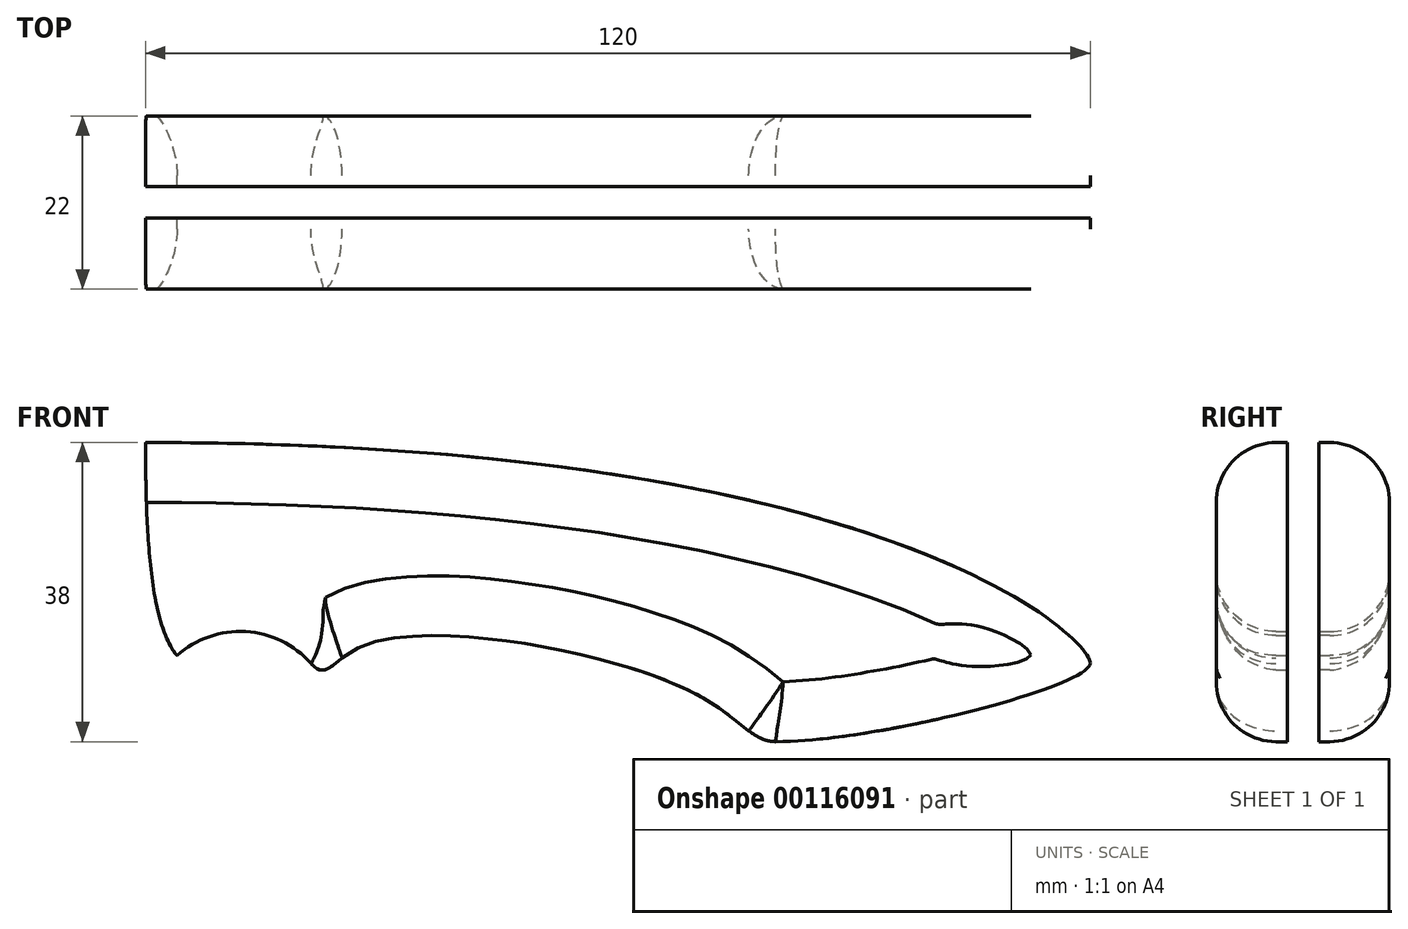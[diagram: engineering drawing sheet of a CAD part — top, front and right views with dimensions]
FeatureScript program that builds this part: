
annotation { "Feature Type Name" : "Feature", "Feature Type Description" : "" }
export const myFeature = defineFeature(function(context is Context, id is Id, definition is map)
    precondition{}
    {
        {
            var Q0;
            Q0=qCreatedBy(makeId("Front.planeOp"),FACE);
            var sketch = newSketch(context, id + "F0", { "sketchPlane" : qUnion([Q0])});
            skLineSegment(sketch, "E0.bottom", {"start": v(0, 0) * mm, "end": v(230, 0) * mm});
            skLineSegment(sketch, "E0.top", {"start": v(0, -38) * mm, "end": v(230, -38) * mm});
            skLineSegment(sketch, "E0.left", {"start": v(0, 0) * mm, "end": v(0, -38) * mm});
            skLineSegment(sketch, "E0.right", {"start": v(230, 0) * mm, "end": v(230, -38) * mm});
            skSolve(sketch);
        }
        {
            var Q0;
            Q0=makeQuery(id+"F0.imprint","IMPRINT",FACE,{"disambiguationData":[TD([[makeQuery(id+"F0.imprint","IMPRINT",EDGE,{"derivedFrom":sQuery(id+"F0.wireOp",EDGE,"E0.bottom")}),-1.0]])]});
            var sketch = newSketch(context, id + "F1", { "sketchPlane" : qUnion([Q0])});
            skLineSegment(sketch, "E1", {"start": v(0, 0) * mm, "end": v(0, -12) * mm});
            skLineSegment(sketch, "E2", {"start": v(110, 0) * mm, "end": v(230, 0) * mm});
            skFitSpline(sketch, "E3", {"points": [v(0, -12) * mm, v(110, 0) * mm], "startDerivative": vector(36.23, 12.3) * mm, "endDerivative": vector(240, 0) * mm});
            skFitSpline(sketch, "E4", {"points": [v(0, -12) * mm, v(110, -38) * mm], "startDerivative": vector(39.03, -50.57) * mm, "endDerivative": vector(165, 0) * mm});
            skFitSpline(sketch, "E5", {"points": [v(110, 0) * mm, v(230, -28) * mm], "startDerivative": vector(285, 0) * mm, "endDerivative": vector(0, -9) * mm});
            skLineSegment(sketch, "E6", {"start": v(110, -38) * mm, "end": v(110, -36) * mm});
            skLineSegment(sketch, "E7", {"start": v(110, -36) * mm, "end": v(122, -36) * mm, "construction": true});
            skArc(sketch, "E8", {"start": v(131, -28.06) * mm, "mid": v(117.76, -24.78) * mm, "end": v(110, -36) * mm});
            skLineSegment(sketch, "E9", {"start": v(131, -28.06) * mm, "end": v(132.98, -30.31) * mm});
            skFitSpline(sketch, "E10", {"points": [v(190, -38) * mm, v(180, -32) * mm, v(137, -26.06) * mm, v(131, -28.06) * mm], "startDerivative": vector(-33, 0) * mm, "endDerivative": vector(-29.63, 33.6) * mm});
            skFitSpline(sketch, "E11", {"points": [v(230, -28) * mm, v(190, -38) * mm], "startDerivative": vector(0, -9) * mm, "endDerivative": vector(-39, 0) * mm});
            skLineSegment(sketch, "E12", {"start": v(110, -28.06) * mm, "end": v(131, -28.06) * mm, "construction": true});
            skLineSegment(sketch, "E13", {"start": v(131, -26.06) * mm, "end": v(137, -26.06) * mm, "construction": true});
            skLineSegment(sketch, "E14", {"start": v(131, -28.06) * mm, "end": v(131, -26.06) * mm, "construction": true});
            skLineSegment(sketch, "E15", {"start": v(190, -38) * mm, "end": v(187, -38) * mm});
            skLineSegment(sketch, "E16", {"start": v(190, -32) * mm, "end": v(180, -32) * mm, "construction": true});
            skLineSegment(sketch, "E17", {"start": v(190, -38) * mm, "end": v(190, -32) * mm, "construction": true});
            skLineSegment(sketch, "E18", {"start": v(190, -38) * mm, "end": v(203, -38) * mm, "construction": true});
            skLineSegment(sketch, "E19", {"start": v(190, -38) * mm, "end": v(230, -38) * mm, "construction": true});
            skLineSegment(sketch, "E20", {"start": v(230, -28) * mm, "end": v(230, -25) * mm, "construction": true});
            skLineSegment(sketch, "E21", {"start": v(230, -28) * mm, "end": v(230, -31) * mm, "construction": true});
            skLineSegment(sketch, "E22", {"start": v(230, -28) * mm, "end": v(230, -38) * mm, "construction": true});
            skLineSegment(sketch, "E23", {"start": v(110, 0) * mm, "end": v(30, 0) * mm, "construction": true});
            skLineSegment(sketch, "E24", {"start": v(0, 0) * mm, "end": v(110, 0) * mm, "construction": true});
            skLineSegment(sketch, "E25", {"start": v(110, 0) * mm, "end": v(205, 0) * mm});
            skLineSegment(sketch, "E26", {"start": v(0, -12) * mm, "end": v(12.08, -7.9) * mm});
            skLineSegment(sketch, "E27", {"start": v(0, -12) * mm, "end": v(13.01, -28.86) * mm});
            skLineSegment(sketch, "E28", {"start": v(110, -27.06) * mm, "end": v(114, -27.06) * mm, "construction": true});
            skLineSegment(sketch, "E29", {"start": v(114, -27.06) * mm, "end": v(110, -22.58) * mm, "construction": true});
            skFitSpline(sketch, "E30", {"points": [v(110, 0) * mm, v(114, -27.06) * mm], "startDerivative": vector(0, -21) * mm, "endDerivative": vector(12, -13.42) * mm});
            skLineSegment(sketch, "E31", {"start": v(110, 0) * mm, "end": v(110, -7) * mm, "construction": true});
            skLineSegment(sketch, "E32", {"start": v(110, 0) * mm, "end": v(107, 0) * mm});
            skLineSegment(sketch, "E33", {"start": v(107, 0) * mm, "end": v(97, 0) * mm});
            skLineSegment(sketch, "E34", {"start": v(97, 0) * mm, "end": v(97, -14) * mm});
            skLineSegment(sketch, "E35", {"start": v(97, -14) * mm, "end": v(97, -24) * mm, "construction": true});
            skArc(sketch, "E36", {"start": v(107, -24) * mm, "mid": v(104.07, -16.92) * mm, "end": v(97, -14) * mm});
            skPoint(sketch, "E37", {"position": v(107, -24) * mm});
            skLineSegment(sketch, "E38", {"start": v(107, -24) * mm, "end": v(107, -38) * mm});
            skLineSegment(sketch, "E39", {"start": v(110, -38) * mm, "end": v(55, -38) * mm, "construction": true});
            skSolve(sketch);
        }
        {
            var Q0;
            {var subQ4=sQuery(id+"F1.wireOp",EDGE,"E3");Q0=makeQuery(id+"F1.imprint","IMPRINT",FACE,{"disambiguationData":[TD([[makeQuery(id+"F1.imprint","IMPRINT",EDGE,{"derivedFrom":subQ4}),-1.0]])]});}
            extrude(context, id + "F2", {"entities" : qUnion([Q0]), "endBound" : BoundingType.SYMMETRIC, "depth" : 4 * mm});
        }
        {
            var Q0;
            {var subQ5=sQuery(id+"F1.wireOp",EDGE,"E36");Q0=makeQuery(id+"F1.imprint","IMPRINT",FACE,{"disambiguationData":[TD([[makeQuery(id+"F1.imprint","IMPRINT",EDGE,{"derivedFrom":subQ5}),1.0]])]});}
            extrude(context, id + "F3", {"entities" : qUnion([Q0]), "operationType" : NewBodyOperationType.ADD, "endBound" : BoundingType.SYMMETRIC, "depth" : 4 * mm});
        }
        {
            var Q0;
            Q0=makeQuery(id+"F3.opExtrude","CAP_EDGE",EDGE,{"disambiguationData":[OSD([sQuery(id+"F1.wireOp",EDGE,"E4")])],"isStart":false});
            var Q1;
            Q1=makeQuery(id+"F3.opExtrude","CAP_EDGE",EDGE,{"disambiguationData":[OSD([sQuery(id+"F1.wireOp",EDGE,"E4")])],"isStart":true});
            chamfer(context, id + "F4", {"entities" : qUnion([Q0, Q1]), "chamferType" : ChamferType.TWO_OFFSETS, "width1" : 24 * mm, "oppositeDirection" : false, "width2" : 2 * mm, "tangentPropagation" : true});
        }
        {
            var Q0;
            {var subQ1=sQuery(id+"F1.wireOp",EDGE,"E6");Q0=makeQuery(id+"F1.imprint","IMPRINT",FACE,{"disambiguationData":[TD([[makeQuery(id+"F1.imprint","IMPRINT",EDGE,{"derivedFrom":subQ1}),1.0]])]});}
            var Q1;
            Q1=makeQuery(id+"F1.imprint","IMPRINT",FACE,{"disambiguationData":[TD([[makeQuery(id+"F1.imprint","IMPRINT",EDGE,{"derivedFrom":sQuery(id+"F1.wireOp",EDGE,"E5")}),-1.0]])]});
            extrude(context, id + "F5", {"entities" : qUnion([Q0, Q1]), "operationType" : NewBodyOperationType.ADD, "endBound" : BoundingType.SYMMETRIC, "depth" : 4 * mm});
        }
        {
            var Q0;
            Q0=makeQuery(id+"F1.imprint","IMPRINT",FACE,{"disambiguationData":[TD([[makeQuery(id+"F1.imprint","IMPRINT",EDGE,{"derivedFrom":sQuery(id+"F1.wireOp",EDGE,"E5")}),-1.0]])]});
            extrude(context, id + "F6", {"entities" : qUnion([Q0]), "endBound" : BoundingType.SYMMETRIC, "depth" : 22 * mm});
        }
        {
            var Q0;
            Q0 = qSketchRegion(id + "F0", true);
            extrude(context, id + "F7", {"entities" : qUnion([Q0]), "operationType" : NewBodyOperationType.REMOVE, "endBound" : BoundingType.SYMMETRIC, "oppositeDirection" : true, "depth" : 4 * mm});
        }
        {
            var Q0;
            Q0=makeQuery(id+"F6.opExtrude","CAP_EDGE",EDGE,{"disambiguationData":[OSD([sQuery(id+"F1.wireOp",EDGE,"E5")])],"isStart":false});
            var Q1;
            Q1=makeQuery(id+"F6.opExtrude","CAP_EDGE",EDGE,{"disambiguationData":[OSD([sQuery(id+"F1.wireOp",EDGE,"E5")])],"isStart":true});
            fillet(context, id + "F8", {"entities" : qUnion([Q0, Q1]), "radius" : 7.6 * mm, "tangentPropagation" : true, "allowEdgeOverflow" : false});
        }
    });
